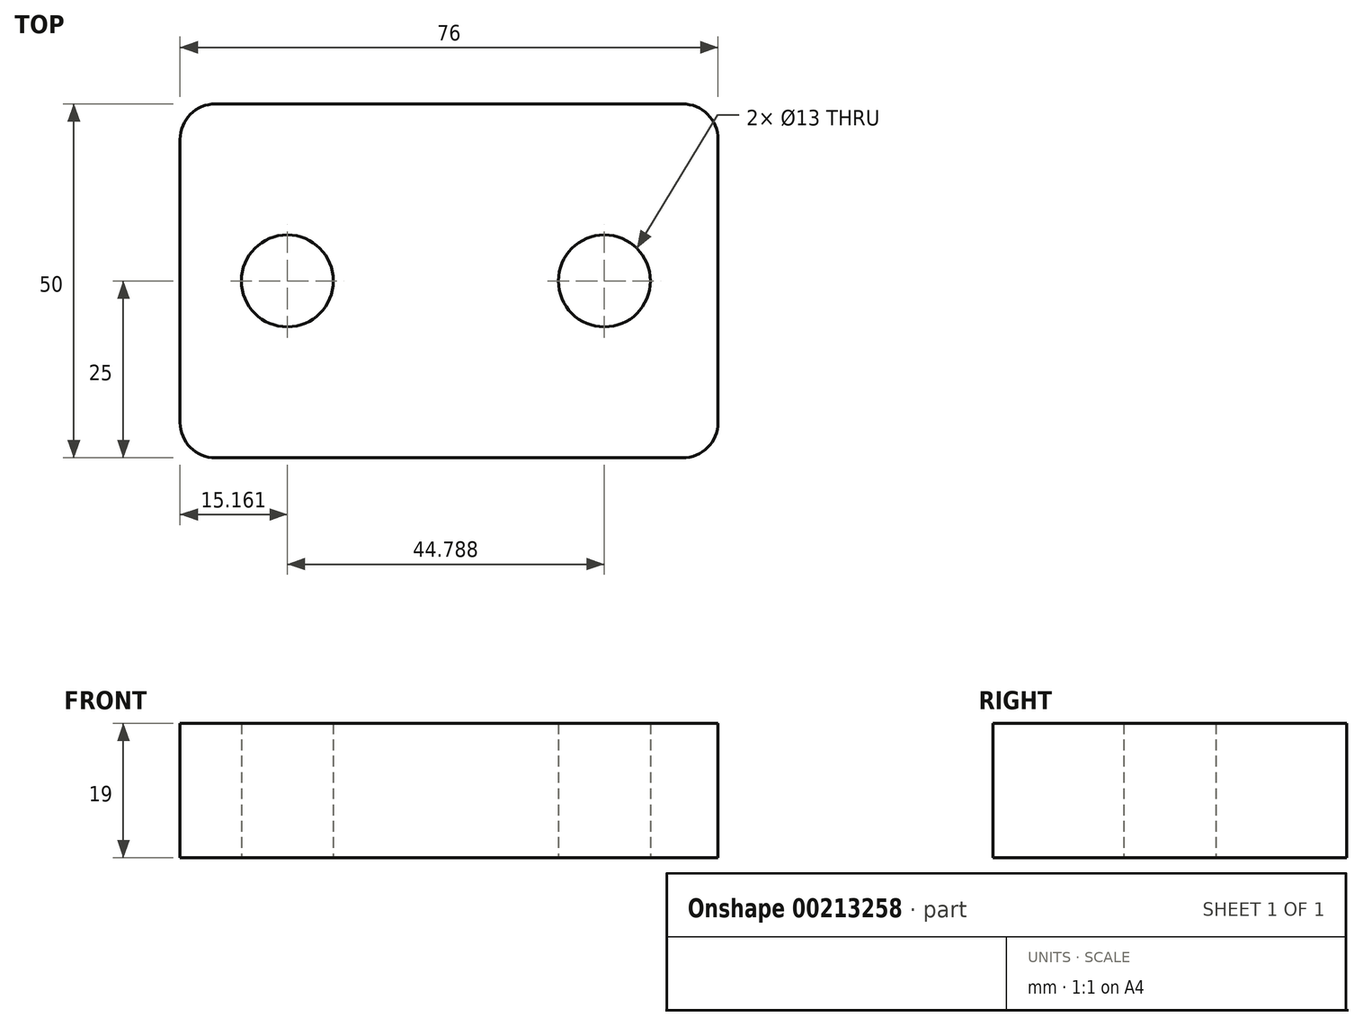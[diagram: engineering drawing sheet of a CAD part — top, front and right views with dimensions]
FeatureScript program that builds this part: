
annotation { "Feature Type Name" : "Feature", "Feature Type Description" : "" }
export const myFeature = defineFeature(function(context is Context, id is Id, definition is map)
    precondition{}
    {
        {
            var Q0;
            Q0=qCreatedBy(makeId("Top.planeOp"),FACE);
            var sketch = newSketch(context, id + "F0", { "sketchPlane" : qUnion([Q0])});
            skLineSegment(sketch, "E0.bottom", {"start": v(33, -25) * mm, "end": v(-33, -25) * mm});
            skLineSegment(sketch, "E0.top", {"start": v(33, 25) * mm, "end": v(-33, 25) * mm});
            skLineSegment(sketch, "E0.left", {"start": v(38, -20) * mm, "end": v(38, 20) * mm});
            skLineSegment(sketch, "E0.right", {"start": v(-38, -20) * mm, "end": v(-38, 20) * mm});
            skPoint(sketch, "E0.middle", {"position": v(0, 0) * mm});
            skCircle(sketch, "E1", {"center": v(-22.84, 0) * mm, "radius": 6.5 * mm});
            skCircle(sketch, "E2", {"center": v(21.95, 0) * mm, "radius": 6.5 * mm});
            skPoint(sketch, "E3.visualSharp", {"position": v(38, 25) * mm});
            skArc(sketch, "E3.filletArc", {"start": v(38, 20) * mm, "mid": v(36.54, 23.54) * mm, "end": v(33, 25) * mm});
            skPoint(sketch, "E4.visualSharp", {"position": v(38, -25) * mm});
            skArc(sketch, "E4.filletArc", {"start": v(33, -25) * mm, "mid": v(36.54, -23.54) * mm, "end": v(38, -20) * mm});
            skPoint(sketch, "E5.visualSharp", {"position": v(-38, -25) * mm});
            skArc(sketch, "E5.filletArc", {"start": v(-38, -20) * mm, "mid": v(-36.54, -23.54) * mm, "end": v(-33, -25) * mm});
            skPoint(sketch, "E6.visualSharp", {"position": v(-38, 25) * mm});
            skArc(sketch, "E6.filletArc", {"start": v(-33, 25) * mm, "mid": v(-36.54, 23.54) * mm, "end": v(-38, 20) * mm});
            skSolve(sketch);
        }
        {
            var Q0;
            Q0=makeQuery(id+"F0.imprint","IMPRINT",FACE,{"disambiguationData":[TD([[makeQuery(id+"F0.imprint","IMPRINT",EDGE,{"derivedFrom":sQuery(id+"F0.wireOp",EDGE,"E0.bottom")}),-1.0]])]});
            extrude(context, id + "F1", {"entities" : qUnion([Q0]), "depth" : 19 * mm});
        }
    });
